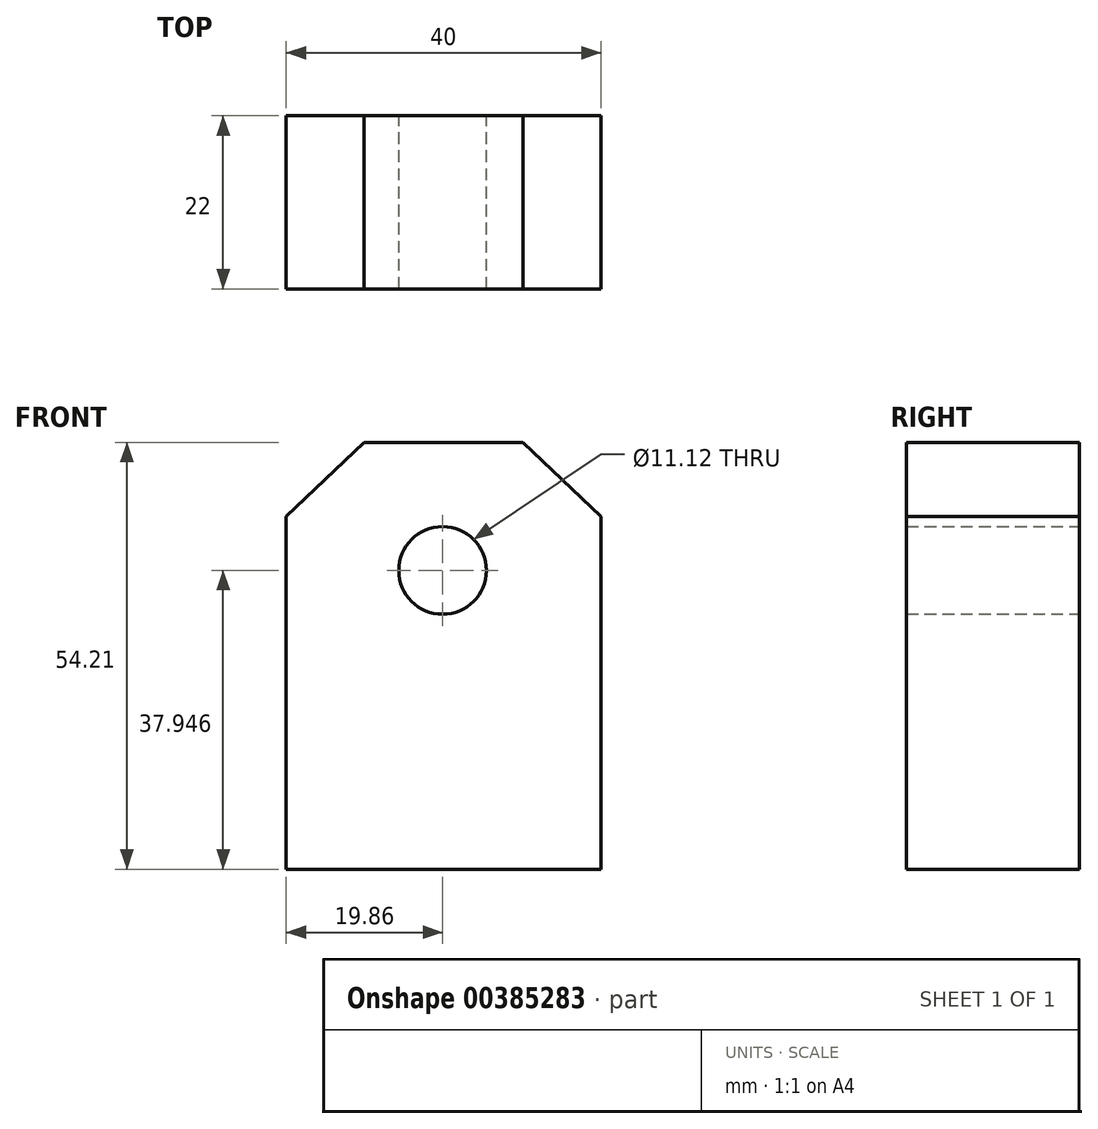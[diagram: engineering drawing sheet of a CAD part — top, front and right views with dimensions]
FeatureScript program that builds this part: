
annotation { "Feature Type Name" : "Feature", "Feature Type Description" : "" }
export const myFeature = defineFeature(function(context is Context, id is Id, definition is map)
    precondition{}
    {
        {
            var Q0;
            Q0=qCreatedBy(makeId("Front.planeOp"),FACE);
            var sketch = newSketch(context, id + "F0", { "sketchPlane" : qUnion([Q0])});
            skLineSegment(sketch, "E0.bottom", {"start": v(-19.86, 0) * mm, "end": v(20.14, 0) * mm});
            skLineSegment(sketch, "E0.left", {"start": v(-19.86, 0) * mm, "end": v(-19.86, 44.8) * mm});
            skLineSegment(sketch, "E0.right", {"start": v(20.14, 0) * mm, "end": v(20.14, 44.8) * mm});
            skCircle(sketch, "E1", {"center": v(0, 37.95) * mm, "radius": 5.56 * mm});
            skLineSegment(sketch, "E2", {"start": v(-19.86, 44.8) * mm, "end": v(-10, 54.21) * mm});
            skLineSegment(sketch, "E3", {"start": v(-10, 54.21) * mm, "end": v(10.21, 54.21) * mm});
            skLineSegment(sketch, "E4", {"start": v(20.14, 44.8) * mm, "end": v(10.21, 54.21) * mm});
            skPoint(sketch, "E5.orphan", {"position": v(-11.6, 52.64) * mm});
            skPoint(sketch, "E6.start.orphan", {"position": v(11.89, 52.64) * mm});
            skSolve(sketch);
        }
        {
            var Q0;
            Q0=makeQuery(id+"F0.imprint","IMPRINT",FACE,{"disambiguationData":[TD([[makeQuery(id+"F0.imprint","IMPRINT",EDGE,{"derivedFrom":sQuery(id+"F0.wireOp",EDGE,"E0.bottom")}),1.0]])]});
            extrude(context, id + "F1", {"entities" : qUnion([Q0]), "depth" : 22 * mm});
        }
    });
